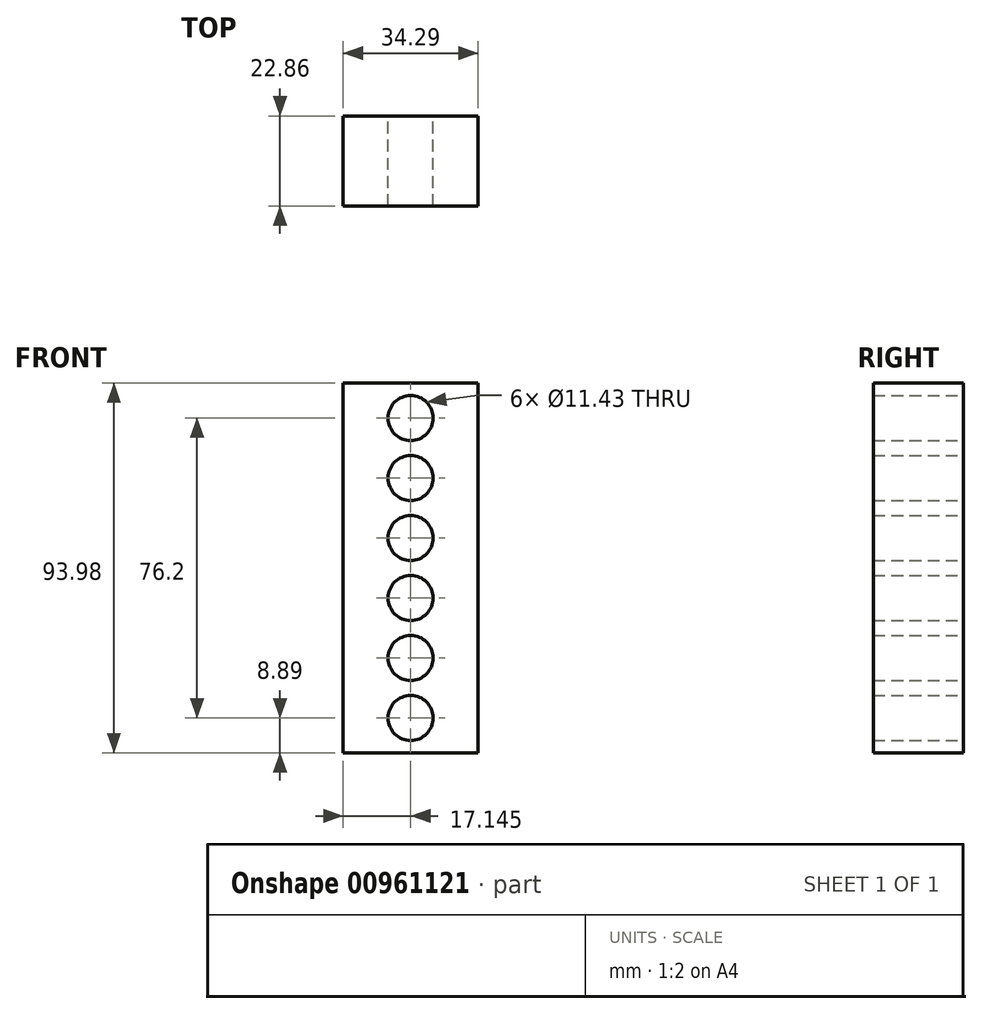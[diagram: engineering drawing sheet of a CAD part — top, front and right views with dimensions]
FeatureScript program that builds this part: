
annotation { "Feature Type Name" : "Feature", "Feature Type Description" : "" }
export const myFeature = defineFeature(function(context is Context, id is Id, definition is map)
    precondition{}
    {
        {
            var Q0;
            Q0=qCreatedBy(makeId("Front.planeOp"),FACE);
            var sketch = newSketch(context, id + "F0", { "sketchPlane" : qUnion([Q0])});
            skLineSegment(sketch, "E0.bottom", {"start": v(0, 0) * mm, "end": v(34.3, 0) * mm});
            skLineSegment(sketch, "E0.top", {"start": v(0, 93.98) * mm, "end": v(34.3, 93.98) * mm});
            skLineSegment(sketch, "E0.left", {"start": v(0, 0) * mm, "end": v(0, 93.98) * mm});
            skLineSegment(sketch, "E0.right", {"start": v(34.3, 0) * mm, "end": v(34.3, 93.98) * mm});
            skLineSegment(sketch, "E1", {"start": v(17.14, 93.98) * mm, "end": v(17.15, 0) * mm});
            skCircle(sketch, "E2", {"center": v(17.15, 69.85) * mm, "radius": 5.72 * mm});
            skCircle(sketch, "E3", {"center": v(17.15, 54.61) * mm, "radius": 5.72 * mm});
            skCircle(sketch, "E4", {"center": v(17.15, 39.37) * mm, "radius": 5.72 * mm});
            skCircle(sketch, "E5", {"center": v(17.15, 24.13) * mm, "radius": 5.72 * mm});
            skCircle(sketch, "E6", {"center": v(17.15, 8.9) * mm, "radius": 5.72 * mm});
            skCircle(sketch, "E7", {"center": v(17.14, 85.1) * mm, "radius": 5.72 * mm});
            skSolve(sketch);
        }
        {
            var Q0;
            Q0=makeQuery(id+"F0.imprint","IMPRINT",FACE,{"disambiguationData":[TD([[makeQuery(id+"F0.imprint","IMPRINT",EDGE,{"derivedFrom":sQuery(id+"F0.wireOp",EDGE,"E0.bottom")}),1.0]])]});
            extrude(context, id + "F1", {"entities" : qUnion([Q0]), "depth" : 22.86 * mm, "offsetDistance" : 25.4 * mm});
        }
    });
